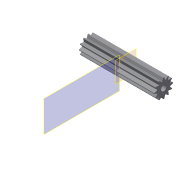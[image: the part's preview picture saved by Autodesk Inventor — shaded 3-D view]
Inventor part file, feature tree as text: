
AUTODESK INVENTOR PART (.ipt)
format: ipt  version: 2019.4 (Build 234330000, 330)  size: 252,928 bytes
history: native  units: mm
features: extrude x3, sketch x3, plane x2, other x2, fillet x1, pattern_circular x1, reference x1, projected_geometry x1
ambient origin geometry x8: Origin, YZ Plane, XZ Plane, XY Plane, X Axis, Y Axis, Z Axis, Center Point
bodies: Solid1 (feature_tree)
feature tree (14):
  plane  "Work Plane1"
  extrude  "Extrusion1"  Depth=19.198622mm
  fillet  "Fillet1"  Radius=0.2mm
  pattern_circular  "Circular Pattern2"  Count=4  [1 undecoded]
  plane  "Work Plane2"
  extrude  "Extrusion2"  Depth=10.0mm TaperAngle=360.0deg
  extrude  "Extrusion3"  Depth=10.0mm
  sketch  "Sketch1"  dims[d0=0.15mm d1=19.198622mm d2=0.2mm]
  reference  "Reference1"
  sketch  "Sketch2"  dims[d3=90.0deg d5=40.0mm d6=0.0mm]
  projected_geometry  "Projected Loop1"
  sketch  "Sketch4"  dims[d10=0.3mm d11=120.0mm d12=360.0deg d14=2.8mm d15=5.0mm d16=0.0mm d20=4.0mm d21=10.0mm d22=0.0mm]
  other  "Assembly_Cube_Z_Focus_MGN_NEMA_v3.iam"
  other  "30_Cube_Z_Focus_MGN12_manual_slide:1"
note: 1 required parameter value undecoded (feature->parameter linkage not recoverable at this tier; creation-order binding heuristic only, values carry confidence <= 0.55)
